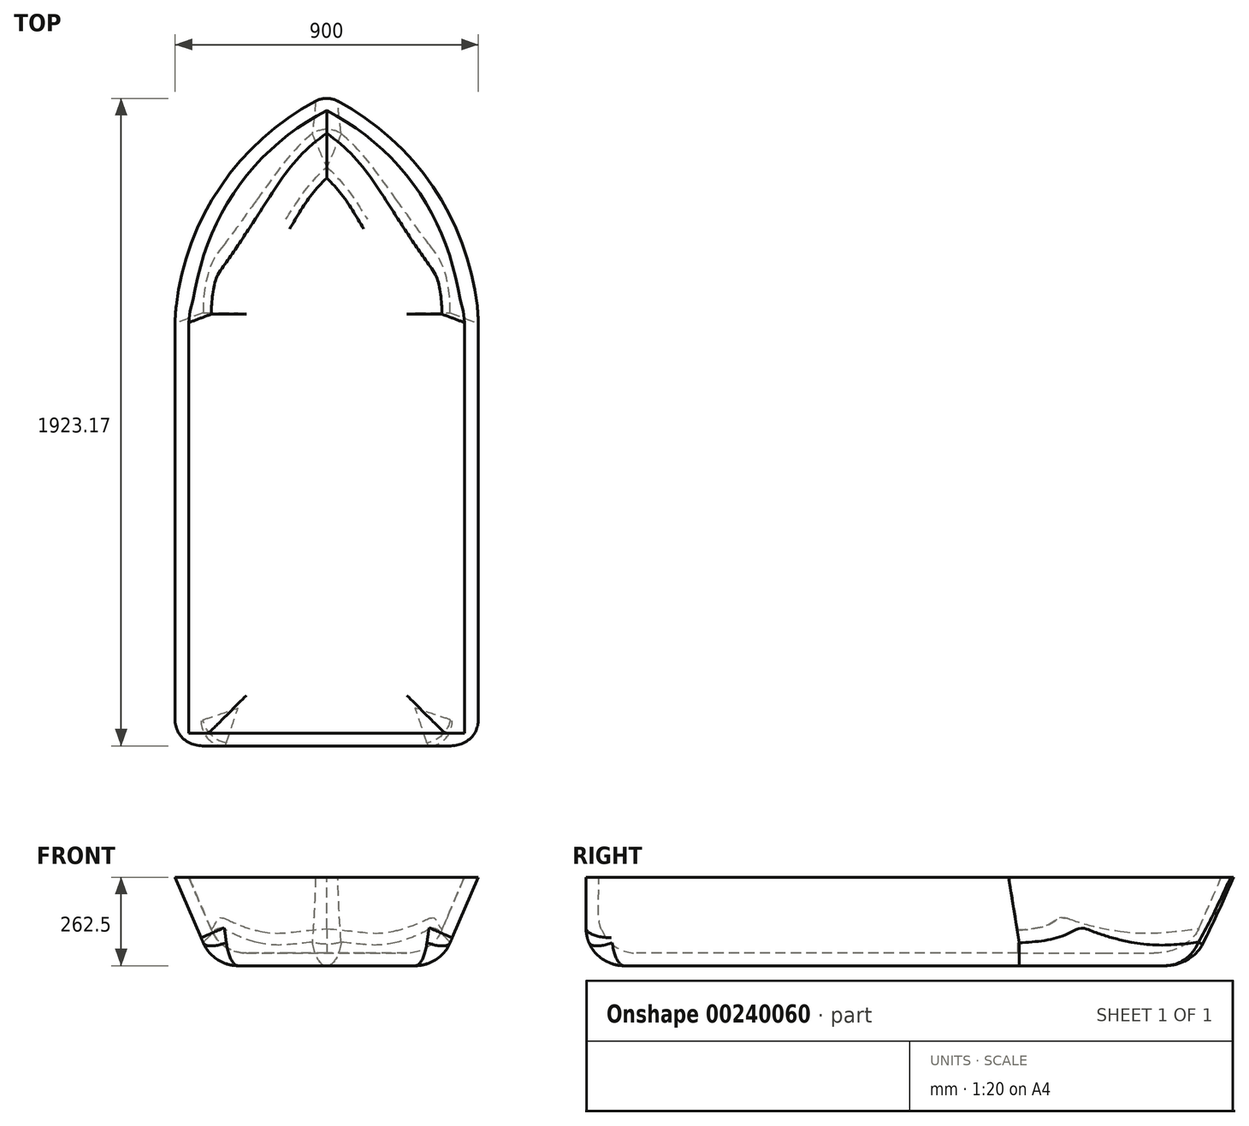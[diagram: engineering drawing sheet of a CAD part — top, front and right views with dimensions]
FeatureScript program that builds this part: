
annotation { "Feature Type Name" : "Feature", "Feature Type Description" : "" }
export const myFeature = defineFeature(function(context is Context, id is Id, definition is map)
    precondition{}
    {
        {
            var Q0;
            Q0=qCreatedBy(makeId("Top.planeOp"),FACE);
            var sketch = newSketch(context, id + "F0", { "sketchPlane" : qUnion([Q0])});
            skArc(sketch, "E0", {"start": v(0, 82.35) * mm, "mid": v(-20.3, 65.36) * mm, "end": v(-29.8, 40.67) * mm});
            skLineSegment(sketch, "E1", {"start": v(-30, 37.24) * mm, "end": v(-30, -46.4) * mm});
            skLineSegment(sketch, "E2", {"start": v(-30, -46.4) * mm, "end": v(0, -46.4) * mm});
            skArc(sketch, "E3.MirrorCS", {"start": v(-1.59, 83.07) * mm, "mid": v(19.78, 66.07) * mm, "end": v(29.8, 40.67) * mm});
            skLineSegment(sketch, "E4.MirrorCS", {"start": v(30, 37.24) * mm, "end": v(30, -46.4) * mm});
            skLineSegment(sketch, "E5.MirrorCS", {"start": v(30, -46.4) * mm, "end": v(0, -46.4) * mm});
            skPoint(sketch, "E6.visualSharp", {"position": v(-30, 38.6) * mm});
            skArc(sketch, "E6.filletArc", {"start": v(-29.8, 40.67) * mm, "mid": v(-29.95, 38.96) * mm, "end": v(-30, 37.24) * mm});
            skPoint(sketch, "E7.visualSharp", {"position": v(30, 38.6) * mm});
            skArc(sketch, "E7.filletArc", {"start": v(30, 37.24) * mm, "mid": v(29.95, 38.96) * mm, "end": v(29.8, 40.67) * mm});
            skSolve(sketch);
        }
        {
            var Q0;
            Q0=qCreatedBy(makeId("Top.planeOp"),FACE);
            cPlane(context, id + "F1", {"entities" : qUnion([Q0]), "cplaneType" : CPlaneType.OFFSET, "offset" : 17.5 * mm, "oppositeDirection" : true, "width" : 150 * mm, "height" : 150 * mm});
        }
        {
            var Q0;
            Q0=qCreatedBy(id+"F1.planeOp",FACE);
            var sketch = newSketch(context, id + "F2", { "sketchPlane" : qUnion([Q0])});
            skLineSegment(sketch, "E8", {"start": v(-22.5, -46.43) * mm, "end": v(22.5, -46.43) * mm});
            skLineSegment(sketch, "E9", {"start": v(22.5, -46.43) * mm, "end": v(22.5, 40.07) * mm});
            skLineSegment(sketch, "E10", {"start": v(13.71, 61.29) * mm, "end": v(0, 75) * mm});
            skLineSegment(sketch, "E11", {"start": v(0, 75) * mm, "end": v(-13.71, 61.29) * mm});
            skLineSegment(sketch, "E12", {"start": v(-22.5, 40.07) * mm, "end": v(-22.5, -46.43) * mm});
            skPoint(sketch, "E13.visualSharp", {"position": v(-22.5, 52.5) * mm});
            skArc(sketch, "E13.filletArc", {"start": v(-13.71, 61.29) * mm, "mid": v(-20.22, 51.55) * mm, "end": v(-22.5, 40.07) * mm});
            skPoint(sketch, "E14.visualSharp", {"position": v(22.5, 52.5) * mm});
            skArc(sketch, "E14.filletArc", {"start": v(22.5, 40.07) * mm, "mid": v(20.22, 51.55) * mm, "end": v(13.71, 61.29) * mm});
            skSolve(sketch);
        }
        {
            var Q0;
            Q0=makeQuery(id+"F2.imprint","IMPRINT",FACE,{"disambiguationData":[TD([[makeQuery(id+"F2.imprint","IMPRINT",EDGE,{"derivedFrom":sQuery(id+"F2.wireOp",EDGE,"E8")}),1.0]])]});
            var Q1;
            Q1=makeQuery(id+"F0.imprint","IMPRINT",FACE,{"disambiguationData":[TD([[makeQuery(id+"F0.imprint","IMPRINT",EDGE,{"derivedFrom":sQuery(id+"F0.wireOp",EDGE,"E0")}),1.0]])]});
            loft(context, id + "F3", {"sheetProfilesArray" : [{ "sheetProfileEntities" : qUnion([Q0]) }, { "sheetProfileEntities" : qUnion([Q1]) }]});
        }
        {
            var Q0;
            Q0=makeQuery(id+"F3.opLoft","CAP_FACE",FACE,{"disambiguationData":[OSD([makeQuery(id+"F0.imprint","IMPRINT",FACE,{"disambiguationData":[TD([[makeQuery(id+"F0.imprint","IMPRINT",EDGE,{"derivedFrom":sQuery(id+"F0.wireOp",EDGE,"E0")}),1.0]])]})])],"isStart":true});
            shell(context, id + "F4", {"entities" : qUnion([Q0]), "thickness" : 2.5 * mm});
        }
        {
            var Q0;
            Q0=makeQuery(id+"F3.opLoft","SWEPT_EDGE",EDGE,{"disambiguationData":[OSD([sQuery(id+"F0.wireOp",EDGE,"E1"),sQuery(id+"F0.wireOp",EDGE,"E2"),sQuery(id+"F2.wireOp",EDGE,"E8"),sQuery(id+"F2.wireOp",EDGE,"E12")])]});
            var Q1;
            Q1=makeQuery(id+"F3.opLoft","SWEPT_EDGE",EDGE,{"disambiguationData":[OSD([sQuery(id+"F0.wireOp",EDGE,"E4.MirrorCS"),sQuery(id+"F0.wireOp",EDGE,"E5.MirrorCS"),sQuery(id+"F2.wireOp",EDGE,"E8"),sQuery(id+"F2.wireOp",EDGE,"E9")])]});
            var Q2;
            Q2=makeQuery(id+"F3.opLoft","SWEPT_EDGE",EDGE,{"disambiguationData":[OSD([sQuery(id+"F0.wireOp",EDGE,"E3.MirrorCS"),sQuery(id+"F0.wireOp",EDGE,"E4.MirrorCS"),sQuery(id+"F2.wireOp",EDGE,"E9"),sQuery(id+"F2.wireOp",EDGE,"E10")])]});
            var Q3;
            Q3=makeQuery(id+"F3.opLoft","SWEPT_EDGE",EDGE,{"disambiguationData":[OSD([sQuery(id+"F0.wireOp",EDGE,"E0"),sQuery(id+"F0.wireOp",EDGE,"E1"),sQuery(id+"F2.wireOp",EDGE,"E11"),sQuery(id+"F2.wireOp",EDGE,"E12")])]});
            fillet(context, id + "F5", {"entities" : qUnion([Q0, Q1, Q2, Q3]), "radius" : 5 * mm, "tangentPropagation" : true, "allowEdgeOverflow" : false});
        }
        {
            var Q0;
            Q0=makeQuery(id+"F4.opShell","OFFSET_FACE",FACE,{"disambiguationData":[OSD([makeQuery(id+"F2.imprint","IMPRINT",FACE,{"disambiguationData":[TD([[makeQuery(id+"F2.imprint","IMPRINT",EDGE,{"derivedFrom":sQuery(id+"F2.wireOp",EDGE,"E8")}),1.0]])]})])]});
            var Q1;
            Q1=makeQuery(id+"F3.opLoft","CAP_FACE",FACE,{"disambiguationData":[OSD([makeQuery(id+"F2.imprint","IMPRINT",FACE,{"disambiguationData":[TD([[makeQuery(id+"F2.imprint","IMPRINT",EDGE,{"derivedFrom":sQuery(id+"F2.wireOp",EDGE,"E8")}),1.0]])]})])],"isStart":true});
            fillet(context, id + "F6", {"entities" : qUnion([Q0, Q1]), "radius" : 7.5 * mm, "tangentPropagation" : true, "allowEdgeOverflow" : false});
        }
        {
            var Q0;
            {var subQ1=sQuery(id+"F0.wireOp",EDGE,"E0");Q0=makeQuery(id+"F3.opLoft","SWEPT_BODY",BODY,{"disambiguationData":[OSD([makeQuery(id+"F0.imprint","IMPRINT",FACE,{"disambiguationData":[TD([[makeQuery(id+"F0.imprint","IMPRINT",EDGE,{"derivedFrom":subQ1}),1.0]])]}),makeQuery(id+"F2.imprint","IMPRINT",FACE,{"disambiguationData":[TD([[makeQuery(id+"F2.imprint","IMPRINT",EDGE,{"derivedFrom":sQuery(id+"F2.wireOp",EDGE,"E8")}),1.0]])]})])]});}
            var Q1;
            Q1=qCreatedBy(makeId("Origin.pointOp"),VERTEX);
            transform(context, id + "F7", {"entities" : qUnion([Q0]), "transformType" : TransformType.SCALE_UNIFORMLY, "scale" : 15, "scalePoint" : qUnion([Q1]), "makeCopy" : false});
        }
    });
